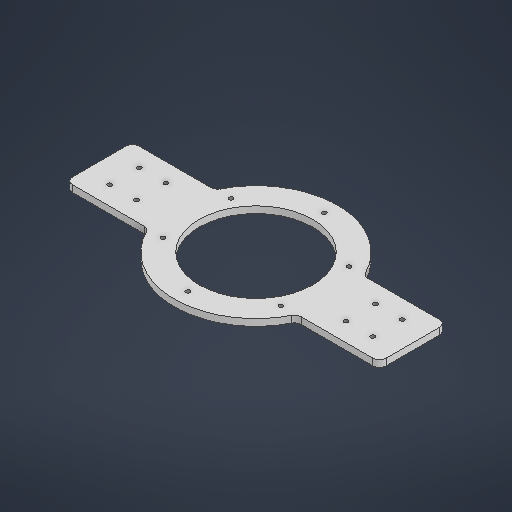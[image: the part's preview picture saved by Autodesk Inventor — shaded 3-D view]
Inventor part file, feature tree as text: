
AUTODESK INVENTOR PART (.ipt)
format: ipt  version: 2025 (Build 290162000, 162)  size: 272,384 bytes
history: native  units: in
note: dims shown in document units (in); Inventor stores cm internally (conversion verified against a paired STEP export)
features: sketch x4, hole x2, extrude x1, fillet x1
ambient origin geometry x8: Origin, YZ Plane, XZ Plane, XY Plane, X Axis, Y Axis, Z Axis, Center Point
bodies: Solid1 (feature_tree)
feature tree (8):
  extrude  "Extrusion1"  Depth=0.1969in TaperAngle=0.0deg
  hole  "Hole1"  [1 undecoded]
  hole  "Hole2"  [1 undecoded]
  fillet  "Fillet2"  Radius=2.3622in
  sketch  "Sketch1"  dims[d0=3.3465in d3=0.1969in d4=0.0in]
  sketch  "Sketch2"  dims[d33=4.0157in d34=0.1575in d35=2.3622in d37=360.0deg]
  sketch  "Sketch3"  dims[d39=0.1276in d40=0.315in d41=0.1575in d42=0.0787in d43=90.0deg d44=0.4646in d45=0.8108in d46=9.252in d47=1.9685in d51=0.1575in d52=0.748in d53=0.5512in d54=0.1575in d55=0.7874in d56=0.1969in]
  sketch  "Sketch Circular Pattern1"  dims[d11=0.1276in d12=0.315in d13=0.1575in d14=0.0787in d15=90.0deg d16=0.4646in d17=0.8108in d29=2.4016in]
note: 2 required parameter values undecoded (feature->parameter linkage not recoverable at this tier; creation-order binding heuristic only, values carry confidence <= 0.55)
